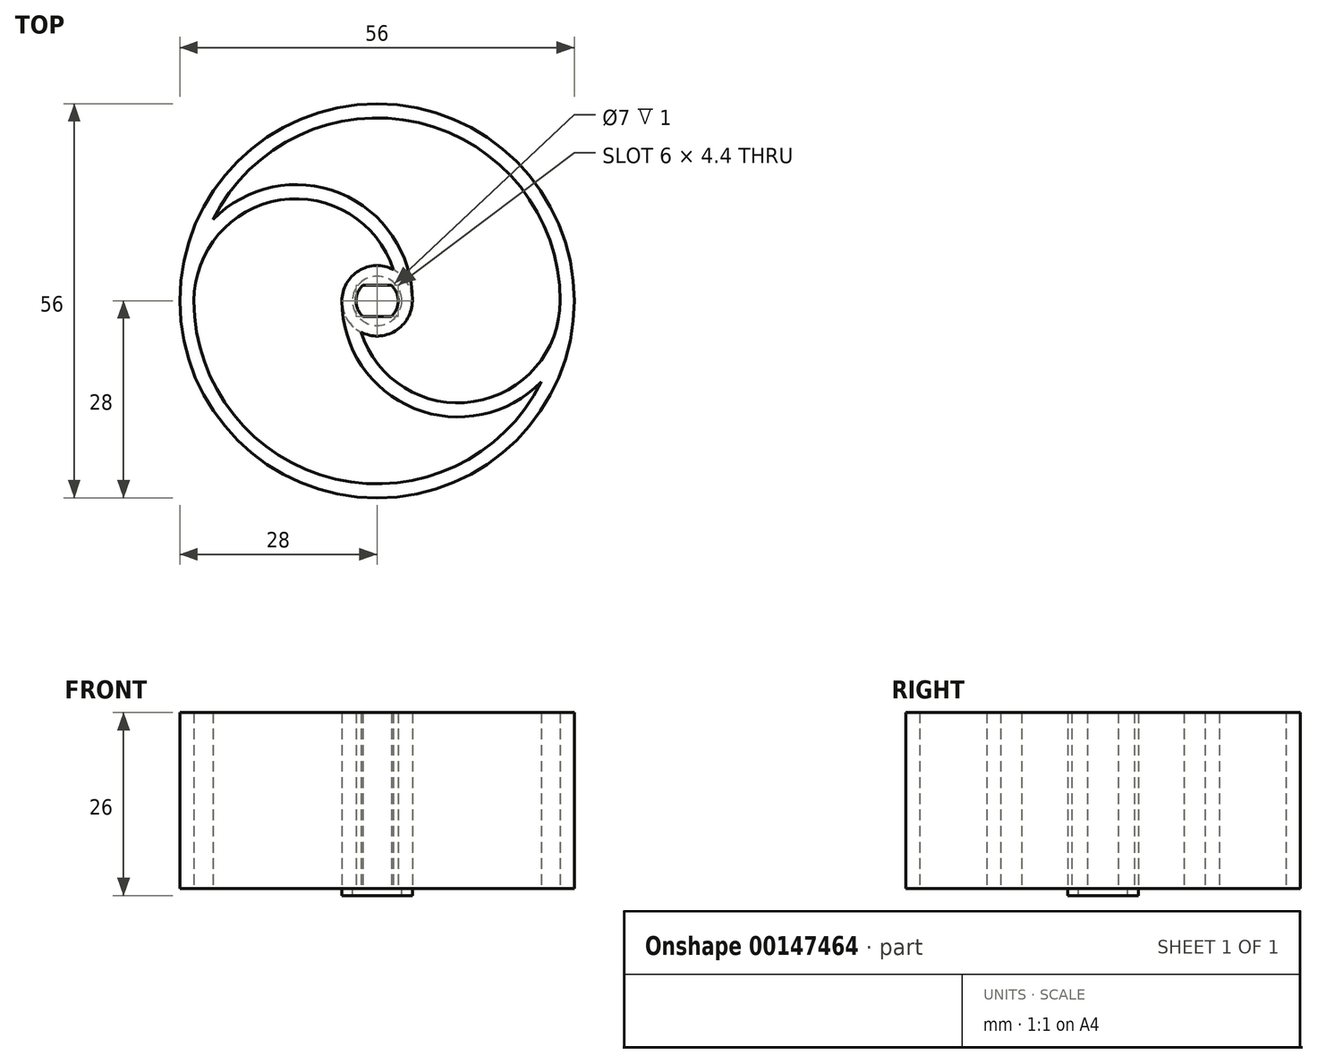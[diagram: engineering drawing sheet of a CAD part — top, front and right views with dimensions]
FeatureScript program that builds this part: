
annotation { "Feature Type Name" : "Feature", "Feature Type Description" : "" }
export const myFeature = defineFeature(function(context is Context, id is Id, definition is map)
    precondition{}
    {
        {
            var Q0;
            Q0=qCreatedBy(makeId("Top.planeOp"),FACE);
            var sketch = newSketch(context, id + "F0", { "sketchPlane" : qUnion([Q0])});
            skCircle(sketch, "E0", {"center": v(0, 0) * mm, "radius": 28 * mm});
            skArc(sketch, "E1", {"start": v(-26, 0) * mm, "mid": v(-5.92, -25.32) * mm, "end": v(23.3, -11.53) * mm});
            skPoint(sketch, "E2", {"position": v(0, 26) * mm});
            skPoint(sketch, "E3", {"position": v(-26, 0) * mm});
            skPoint(sketch, "E4", {"position": v(26, 0) * mm});
            skPoint(sketch, "E5", {"position": v(0, -26) * mm});
            skPoint(sketch, "E6", {"position": v(-18.38, -18.38) * mm});
            skPoint(sketch, "E7", {"position": v(18.38, -18.38) * mm});
            skPoint(sketch, "E8", {"position": v(18.38, 18.38) * mm});
            skPoint(sketch, "E9", {"position": v(-18.38, 18.38) * mm});
            skArc(sketch, "E10", {"start": v(2.3, 4.44) * mm, "mid": v(-2.6, 4.27) * mm, "end": v(-5, 0) * mm});
            skLineSegment(sketch, "E11", {"start": v(5, 0) * mm, "end": v(-28, 0) * mm, "construction": true});
            skArc(sketch, "E12", {"start": v(5, 0) * mm, "mid": v(-5.28, 15.28) * mm, "end": v(-23.3, 11.53) * mm});
            skLineSegment(sketch, "E13", {"start": v(-5, 0) * mm, "end": v(28, 0) * mm, "construction": true});
            skArc(sketch, "E14.trimOffspring", {"start": v(26, 0) * mm, "mid": v(5.92, 25.32) * mm, "end": v(-23.3, 11.53) * mm});
            skArc(sketch, "E15.trimOffspring", {"start": v(-2.3, -4.44) * mm, "mid": v(13.75, -14.33) * mm, "end": v(26, 0) * mm});
            skArc(sketch, "E16.trimOffspring", {"start": v(-5, 0) * mm, "mid": v(5.28, -15.28) * mm, "end": v(23.3, -11.53) * mm});
            skArc(sketch, "E17.trimOffspring", {"start": v(2.3, 4.44) * mm, "mid": v(-13.75, 14.33) * mm, "end": v(-26, 0) * mm});
            skArc(sketch, "E18.trimOffspring", {"start": v(-2.3, -4.44) * mm, "mid": v(2.6, -4.27) * mm, "end": v(5, 0) * mm});
            skSolve(sketch);
        }
        {
            var Q0;
            Q0=makeQuery(id+"F0.imprint","IMPRINT",FACE,{"disambiguationData":[TD([[makeQuery(id+"F0.imprint","IMPRINT",EDGE,{"derivedFrom":sQuery(id+"F0.wireOp",EDGE,"E0")}),1.0]])]});
            extrude(context, id + "F1", {"entities" : qUnion([Q0]), "depth" : 25 * mm});
        }
        {
            var Q0;
            Q0=qCreatedBy(makeId("Top.planeOp"),FACE);
            var sketch = newSketch(context, id + "F2", { "sketchPlane" : qUnion([Q0])});
            skCircle(sketch, "E19", {"center": v(0, 0) * mm, "radius": 3 * mm});
            skLineSegment(sketch, "E20.bottom", {"start": v(-2.04, -2.2) * mm, "end": v(2.04, -2.2) * mm});
            skLineSegment(sketch, "E20.top", {"start": v(-2.04, 2.2) * mm, "end": v(2.04, 2.2) * mm});
            skLineSegment(sketch, "E20.left", {"start": v(-2.04, -2.2) * mm, "end": v(-2.04, 2.2) * mm});
            skLineSegment(sketch, "E20.right", {"start": v(2.04, -2.2) * mm, "end": v(2.04, 2.2) * mm});
            skSolve(sketch);
        }
        {
            var Q0;
            {var subQ0=sQuery(id+"F2.wireOp",EDGE,"E20.left");Q0=makeQuery(id+"F2.imprint","IMPRINT",FACE,{"disambiguationData":[TD([[makeQuery(id+"F2.imprint","IMPRINT",EDGE,{"derivedFrom":subQ0}),1.0]])]});}
            var Q1;
            Q1=makeQuery(id+"F2.imprint","IMPRINT",FACE,{"disambiguationData":[TD([[makeQuery(id+"F2.imprint","IMPRINT",EDGE,{"derivedFrom":sQuery(id+"F2.wireOp",EDGE,"E20.bottom")}),1.0]])]});
            var Q2;
            {var subQ0=sQuery(id+"F2.wireOp",EDGE,"E20.right");Q2=makeQuery(id+"F2.imprint","IMPRINT",FACE,{"disambiguationData":[TD([[makeQuery(id+"F2.imprint","IMPRINT",EDGE,{"derivedFrom":subQ0}),-1.0]])]});}
            extrude(context, id + "F3", {"entities" : qUnion([Q0, Q1, Q2]), "operationType" : NewBodyOperationType.REMOVE, "depth" : 30 * mm});
        }
        {
            var Q0;
            Q0=qCreatedBy(makeId("Top.planeOp"),FACE);
            var sketch = newSketch(context, id + "F4", { "sketchPlane" : qUnion([Q0])});
            skCircle(sketch, "E21", {"center": v(0, 0) * mm, "radius": 5 * mm});
            skCircle(sketch, "E22", {"center": v(0, 0) * mm, "radius": 3.5 * mm});
            skSolve(sketch);
        }
        {
            var Q0;
            Q0=qSketchRegion(id+"F4",true);
            extrude(context, id + "F5", {"entities" : qUnion([Q0]), "operationType" : NewBodyOperationType.ADD, "oppositeDirection" : true, "depth" : 1 * mm});
        }
    });
